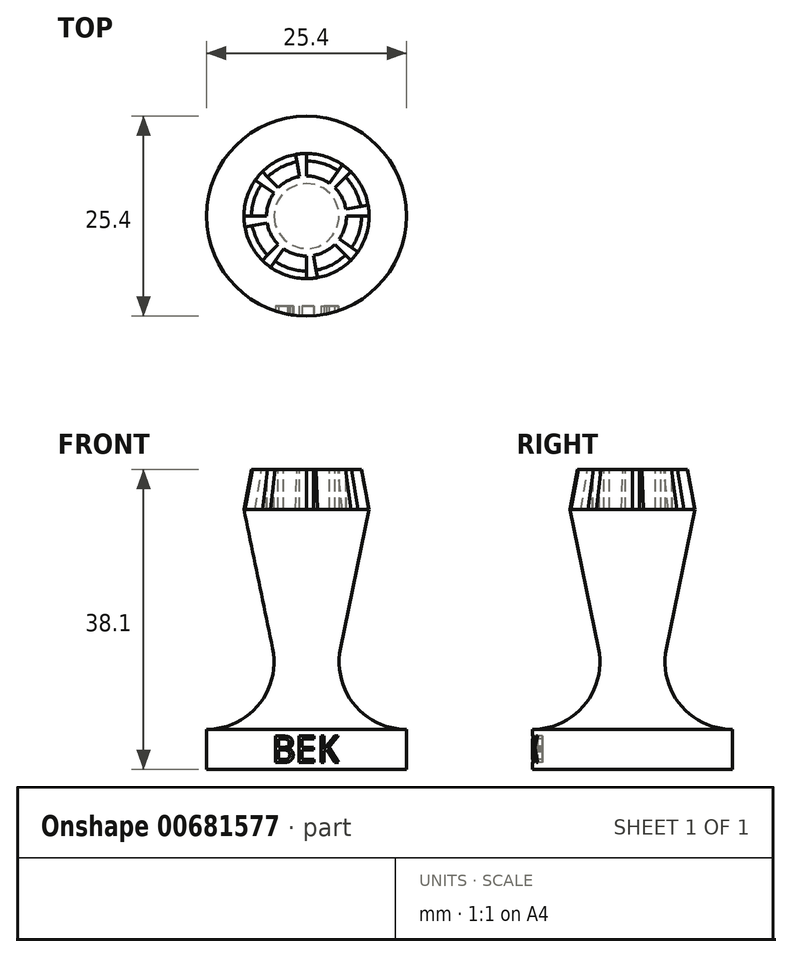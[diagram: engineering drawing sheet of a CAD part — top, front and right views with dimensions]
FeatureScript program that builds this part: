
annotation { "Feature Type Name" : "Feature", "Feature Type Description" : "" }
export const myFeature = defineFeature(function(context is Context, id is Id, definition is map)
    precondition{}
    {
        {
            var Q0;
            Q0=qCreatedBy(makeId("Front.planeOp"),FACE);
            var sketch = newSketch(context, id + "F0", { "sketchPlane" : qUnion([Q0])});
            skLineSegment(sketch, "E0", {"start": v(0, 0) * mm, "end": v(12.7, 0) * mm});
            skLineSegment(sketch, "E1", {"start": v(12.7, 0) * mm, "end": v(12.7, 5.08) * mm});
            skLineSegment(sketch, "E2", {"start": v(0, 0) * mm, "end": v(0, 38.1) * mm});
            skLineSegment(sketch, "E3", {"start": v(0, 38.1) * mm, "end": v(6.99, 38.1) * mm});
            skLineSegment(sketch, "E4", {"start": v(6.99, 38.1) * mm, "end": v(7.95, 33.02) * mm});
            skLineSegment(sketch, "E5", {"start": v(7.95, 33.02) * mm, "end": v(0, 33.02) * mm, "construction": true});
            skArc(sketch, "E6", {"start": v(4.32, 15.36) * mm, "mid": v(6.07, 8.23) * mm, "end": v(12.7, 5.08) * mm});
            skLineSegment(sketch, "E7", {"start": v(7.95, 33.02) * mm, "end": v(4.32, 15.36) * mm});
            skSolve(sketch);
        }
        {
            var Q0;
            Q0=makeQuery(id+"F0.imprint","IMPRINT",FACE,{"disambiguationData":[TD([[makeQuery(id+"F0.imprint","IMPRINT",EDGE,{"derivedFrom":sQuery(id+"F0.wireOp",EDGE,"E0")}),1.0]])]});
            var Q1;
            Q1=sQuery(id+"F0.wireOp",EDGE,"E2");
            revolve(context, id + "F1", {"entities" : qUnion([Q0]), "axis" : qUnion([Q1]), "revolveType" : RevolveType.FULL});
        }
        {
            var Q0;
            Q0=makeQuery(id+"F1.opRevolve","SWEPT_FACE",FACE,{"disambiguationData":[OSD([sQuery(id+"F0.wireOp",EDGE,"E3")])]});
            var sketch = newSketch(context, id + "F2", { "sketchPlane" : qUnion([Q0])});
            skCircle(sketch, "E8", {"center": v(0, 0) * mm, "radius": 5.08 * mm});
            skArc(sketch, "E9.0", {"start": v(1.38, -7.83) * mm, "mid": v(0.7, -7.92) * mm, "end": v(0, -7.95) * mm});
            skLineSegment(sketch, "E10", {"start": v(0, -5.08) * mm, "end": v(0, -7.95) * mm});
            skLineSegment(sketch, "E11", {"start": v(0.88, -5) * mm, "end": v(1.38, -7.83) * mm});
            skArc(sketch, "E12.1.0", {"start": v(6.51, -4.56) * mm, "mid": v(6.1, -5.11) * mm, "end": v(5.62, -5.62) * mm});
            skLineSegment(sketch, "E12.1.1", {"start": v(3.6, -3.6) * mm, "end": v(5.62, -5.62) * mm});
            skLineSegment(sketch, "E12.1.2", {"start": v(4.16, -2.91) * mm, "end": v(6.51, -4.56) * mm});
            skArc(sketch, "E12.2.0", {"start": v(7.83, 1.38) * mm, "mid": v(7.92, 0.7) * mm, "end": v(7.95, 0) * mm});
            skLineSegment(sketch, "E12.2.1", {"start": v(5.08, 0) * mm, "end": v(7.95, 0) * mm});
            skLineSegment(sketch, "E12.2.2", {"start": v(5, 0.88) * mm, "end": v(7.83, 1.38) * mm});
            skArc(sketch, "E12.3.0", {"start": v(4.56, 6.51) * mm, "mid": v(5.11, 6.1) * mm, "end": v(5.62, 5.62) * mm});
            skLineSegment(sketch, "E12.3.1", {"start": v(3.6, 3.6) * mm, "end": v(5.62, 5.62) * mm});
            skLineSegment(sketch, "E12.3.2", {"start": v(2.91, 4.16) * mm, "end": v(4.56, 6.51) * mm});
            skArc(sketch, "E12.4.0", {"start": v(-1.38, 7.83) * mm, "mid": v(-0.7, 7.92) * mm, "end": v(0, 7.95) * mm});
            skLineSegment(sketch, "E12.4.1", {"start": v(0, 5.08) * mm, "end": v(0, 7.95) * mm});
            skLineSegment(sketch, "E12.4.2", {"start": v(-0.88, 5) * mm, "end": v(-1.38, 7.83) * mm});
            skArc(sketch, "E12.5.0", {"start": v(-6.51, 4.56) * mm, "mid": v(-6.1, 5.11) * mm, "end": v(-5.62, 5.62) * mm});
            skLineSegment(sketch, "E12.5.1", {"start": v(-3.6, 3.6) * mm, "end": v(-5.62, 5.62) * mm});
            skLineSegment(sketch, "E12.5.2", {"start": v(-4.16, 2.91) * mm, "end": v(-6.51, 4.56) * mm});
            skArc(sketch, "E12.6.0", {"start": v(-7.83, -1.38) * mm, "mid": v(-7.92, -0.7) * mm, "end": v(-7.95, 0) * mm});
            skLineSegment(sketch, "E12.6.1", {"start": v(-5.08, 0) * mm, "end": v(-7.95, 0) * mm});
            skLineSegment(sketch, "E12.6.2", {"start": v(-5, -0.88) * mm, "end": v(-7.83, -1.38) * mm});
            skArc(sketch, "E12.7.0", {"start": v(-4.56, -6.51) * mm, "mid": v(-5.11, -6.1) * mm, "end": v(-5.62, -5.62) * mm});
            skLineSegment(sketch, "E12.7.1", {"start": v(-3.6, -3.6) * mm, "end": v(-5.62, -5.62) * mm});
            skLineSegment(sketch, "E12.7.2", {"start": v(-2.91, -4.16) * mm, "end": v(-4.56, -6.51) * mm});
            skSolve(sketch);
        }
        {
            var Q0;
            Q0 = qSketchRegion(id + "F2", true);
            extrude(context, id + "F3", {"entities" : qUnion([Q0]), "operationType" : NewBodyOperationType.REMOVE, "oppositeDirection" : true, "depth" : 5.08 * mm, "offsetDistance" : 25.4 * mm});
        }
        {
            var Q0;
            Q0=qCreatedBy(makeId("Front.planeOp"),FACE);
            cPlane(context, id + "F4", {"entities" : qUnion([Q0]), "cplaneType" : CPlaneType.OFFSET, "offset" : 12.7 * mm, "width" : 152.4 * mm, "height" : 152.4 * mm});
        }
        {
            var Q0;
            Q0=qCreatedBy(id+"F4.planeOp",FACE);
            var sketch = newSketch(context, id + "F5", { "sketchPlane" : qUnion([Q0])});
            skLineSegment(sketch, "E13", {"start": v(-12.7, 0) * mm, "end": v(-12.7, 5.08) * mm});
            skLineSegment(sketch, "E14", {"start": v(12.7, 5.08) * mm, "end": v(12.7, 0) * mm});
            skText(sketch, "E15", { "text": "BEK", "fontName": "DroidSansMono.ttf"});
            const initialGuessF5  = {"E15": [-0.00427, 0.0009, 1, 0, 0.00336]};
            skSetInitialGuess(sketch, initialGuessF5);
            skSolve(sketch);
        }
        {
            var Q0;
            Q0 = qSketchRegion(id + "F5", true);
            extrude(context, id + "F6", {"entities" : qUnion([Q0]), "operationType" : NewBodyOperationType.REMOVE, "oppositeDirection" : true, "depth" : 1.27 * mm, "offsetDistance" : 25.4 * mm});
        }
    });
